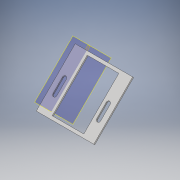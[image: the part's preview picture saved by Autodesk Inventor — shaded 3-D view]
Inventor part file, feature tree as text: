
AUTODESK INVENTOR PART (.ipt)
format: ipt  version: 2019 (Build 230136000, 136)  size: 164,352 bytes
history: native  units: in
note: dims shown in document units (in); Inventor stores cm internally (conversion verified against a paired STEP export)
features: extrude x3, sketch x3, other x3, plane x2, projected_geometry x1
ambient origin geometry x8: Origin, YZ Plane, XZ Plane, XY Plane, X Axis, Y Axis, Z Axis, Center Point
bodies: Body1 (feature_tree)
feature tree (12):
  plane  "Work Plane2"
  plane  "Work Plane3"
  extrude  "Extrusion3"  Depth=0.0787in
  extrude  "Extrusion4"  Depth=0.9094in
  extrude  "Extrusion5"  Depth=0.0787in
  sketch  "Sketch3"  dims[d12=0.0787in d13=0.0787in]
  sketch  "Sketch4"  dims[d14=0.9094in d15=0.6732in]
  projected_geometry  "Projected Loop2"
  sketch  "Sketch5"  dims[d16=0.0787in d17=0.0787in d18=0.0787in d19=0.0787in d20=0.0394in d21=0.0in d22=0.0394in d23=0.0in d24=0.1181in d25=0.1181in d26=0.3937in d27=0.0in d28=1.5827in]
  other  "Assembly_Cube_Dichroic_Beamsplitter_25x35.iam"
  other  "00_Chroma_Dichroic_25x,3x1:1"
  other  "20_Cube_Insert_Beamsplittercube_Base_25x35:1"
